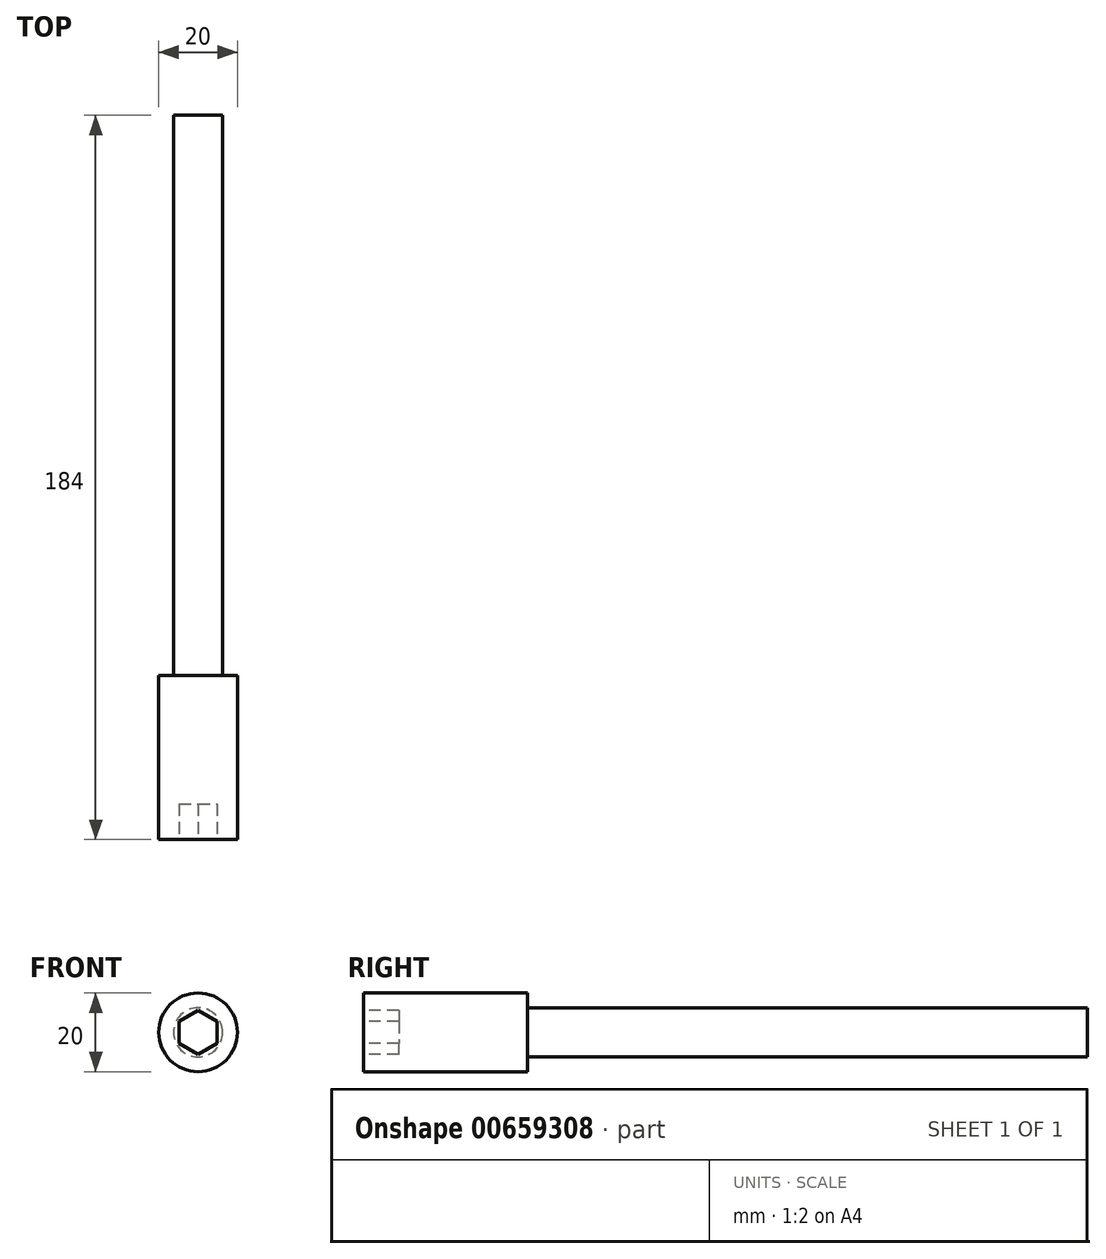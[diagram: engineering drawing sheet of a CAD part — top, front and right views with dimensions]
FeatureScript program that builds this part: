
annotation { "Feature Type Name" : "Feature", "Feature Type Description" : "" }
export const myFeature = defineFeature(function(context is Context, id is Id, definition is map)
    precondition{}
    {
        {
            var Q0;
            Q0=qCreatedBy(makeId("Front.planeOp"),FACE);
            var sketch = newSketch(context, id + "F0", { "sketchPlane" : qUnion([Q0])});
            skCircle(sketch, "E0", {"center": v(0, 0) * mm, "radius": 10 * mm});
            skSolve(sketch);
        }
        {
            var Q0;
            Q0=qSketchRegion(id+"F0",true);
            extrude(context, id + "F1", {"entities" : qUnion([Q0]), "oppositeDirection" : true, "depth" : 41.7 * mm, "offsetDistance" : 25 * mm});
        }
        {
            var Q0;
            Q0=makeQuery(id+"F1.opExtrude","CAP_FACE",FACE,{"disambiguationData":[OSD([sQuery(id+"F0.wireOp",EDGE,"E0")])],"isStart":false});
            var sketch = newSketch(context, id + "F2", { "sketchPlane" : qUnion([Q0])});
            skCircle(sketch, "E1", {"center": v(0, 0) * mm, "radius": 6.25 * mm});
            skSolve(sketch);
        }
        {
            var Q0;
            Q0=qSketchRegion(id+"F2",true);
            extrude(context, id + "F3", {"entities" : qUnion([Q0]), "operationType" : NewBodyOperationType.ADD, "depth" : 142.3 * mm, "offsetDistance" : 25 * mm});
        }
        {
            var Q0;
            Q0=makeQuery(id+"F1.opExtrude","CAP_FACE",FACE,{"disambiguationData":[OSD([sQuery(id+"F0.wireOp",EDGE,"E0")])],"isStart":true});
            var sketch = newSketch(context, id + "F4", { "sketchPlane" : qUnion([Q0])});
            skLineSegment(sketch, "E2.0", {"start": v(4.8, 2.77) * mm, "end": v(4.8, -2.77) * mm});
            skLineSegment(sketch, "E2.1", {"start": v(4.8, -2.77) * mm, "end": v(0, -5.54) * mm});
            skLineSegment(sketch, "E2.2", {"start": v(0, -5.54) * mm, "end": v(-4.8, -2.77) * mm});
            skLineSegment(sketch, "E2.3", {"start": v(-4.8, -2.77) * mm, "end": v(-4.8, 2.77) * mm});
            skLineSegment(sketch, "E2.4", {"start": v(-4.8, 2.77) * mm, "end": v(0, 5.54) * mm});
            skLineSegment(sketch, "E2.5", {"start": v(0, 5.54) * mm, "end": v(4.8, 2.77) * mm});
            skPoint(sketch, "E2.0.midPoint", {"position": v(4.8, 0) * mm});
            skLineSegment(sketch, "E3", {"start": v(0, 9.77) * mm, "end": v(0, -10.26) * mm, "construction": true});
            skCircle(sketch, "E4.0", {"center": v(0, 0) * mm, "radius": 10 * mm, "construction": true});
            skLineSegment(sketch, "E5", {"start": v(-10.58, 0) * mm, "end": v(16.79, 0) * mm, "construction": true});
            skSolve(sketch);
        }
        {
            var Q0;
            Q0=qSketchRegion(id+"F4",true);
            extrude(context, id + "F5", {"entities" : qUnion([Q0]), "operationType" : NewBodyOperationType.REMOVE, "oppositeDirection" : true, "depth" : 9 * mm});
        }
    });
